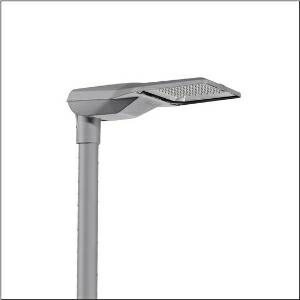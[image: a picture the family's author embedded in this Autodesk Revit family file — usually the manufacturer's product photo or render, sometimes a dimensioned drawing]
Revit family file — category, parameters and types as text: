
# Revit family: streetlight_sl_21_iq_midi___st1_0ab_5xe3m31g08mb_7004
name_source: partatom
category: Lighting Fixtures
units: mm (PartAtom-declared; Revit-internal decimal feet)

## family parameters
Cut with Voids When Loaded = No
Host = Face
Light Source = No
Part Type = Normal
Room Calculation Point = No
Round Connector Dimension = Use Diameter
Shared = No

## types (1)
- --- (1 x LED, 17170 lm, 146.7 W, 3000K)
    Apparent Load = 147 VA
    CIE Flux Codes = 38 73 97 100 100
    Color Rendering = 70
    Color Temperature = 3000K
    Default Elevation = 1800 mm
    Description = Streetlight SL 21 iQ midi, mast luminaire, primary light control with lens, of PMMA, primary optical cover: cover, of toughened safety glass, transparent, light distribution: ST1.0aB, light emission: direct distribution, primary light characteristic: asymmetric, installation type: post-top, side-entry, LED, High Power LED, rated luminous flux: 17.170lm, luminous efficacy: 117lm/W, light colour: 730, colour temperature: 3000K, control gear: iQ Street-Remote, control: Street-Remote, Auto-Match, Temp-Guard, Lumen-Switch, Night-Set, Smart-Wire, Light-Fading, Desk-Remote (wireless, voltage-free reading and setting of iQ features in the workshop via application-optimized NFC function/RFID function), optimised constant luminous flux control (CLO 2.0), pre-setting: linear dimming characteristic, mains connection: 230..240V, AC, 50/60Hz, start of lifetime: 147W, end of service life: 161W, reduction: 62W, luminaire housing, of diecast aluminium, powder-coated, SITECO metallic grey (DB 702S), corrosivity category C5 high according to DIN EN ISO 12944, please order mast flange separately, inclination adjustable: 0°, 5°, 10°, 15°, sealing non-destructively replaceable, multi-level sealing system, length: 644mm, width: 335mm, height: 110mm, mast flange for spigot size: 42mm (side-entry): 5XC10008XM4, 60/48mm (side-entry/post-top): 5XC10108XM2, 76/60mm (side-entry/post-top): 5XC10108XM1, mounting height: 4..8m, protection rating (complete): IP66, insulation class (complete): insulation class II (safety insulation), certification: CE, ENEC, ENEC+, VDE, impact resistance: IK10, permissible operating ambient temperature for outdoor applications: -40..+50°C, standard-compliant lighting for roads and squares, packaging unit: 1 piece

Light Distribution: ST1.0aB
    Height = 111 mm
    Lamp = 1 x LED
    Lamp Light Flux = 17170 lm
    Lamp Power = 146.7 W
    Lamp count = 1
    Length = 644 mm
    Luminous efficacy = 117 lm/W
    Manufacturer = Siteco
    ModVariant = No
    Model = 5XE3M31G08MB
    Number of Poles = 1
    OnlyDefault = Yes
    Power Factor = 1
    Product Name = Streetlight SL 21 iQ midi | ST1.0aB
    Product group = mast luminaire | pylon top
    ProductGroupID = 6100
    Protection Class = Protection class II
    Protection Degree = IP 66
    RLX_Detail_Level = 1
    RLX_Emergency_Light_Flux = 0 lm
    RLX_Emergency_Type = 0
    RLX_Emergency_Type_DB = No
    RlxData = <blob elided: 26933 chars, md5=c2d0b0c6>
    Socket = socket
    Standby Power = 0 W
    System Light Flux = 17170 lm
    System Power = 147 W
    Type Comments = factory setting: luminous flux: 100 % | dim-lin: 254 | 753 mA
    Type Image = l_1004298.jpg
    URL = http://relux.com
    VarID = @adj_180461
    Voltage = 0 V
    Weight = 0.00 kg
    Width = 336 mm

## geometry (parser evidence)
native form markers: Blend x4, Sweep x11
no freeform markers — native parametric forms only
